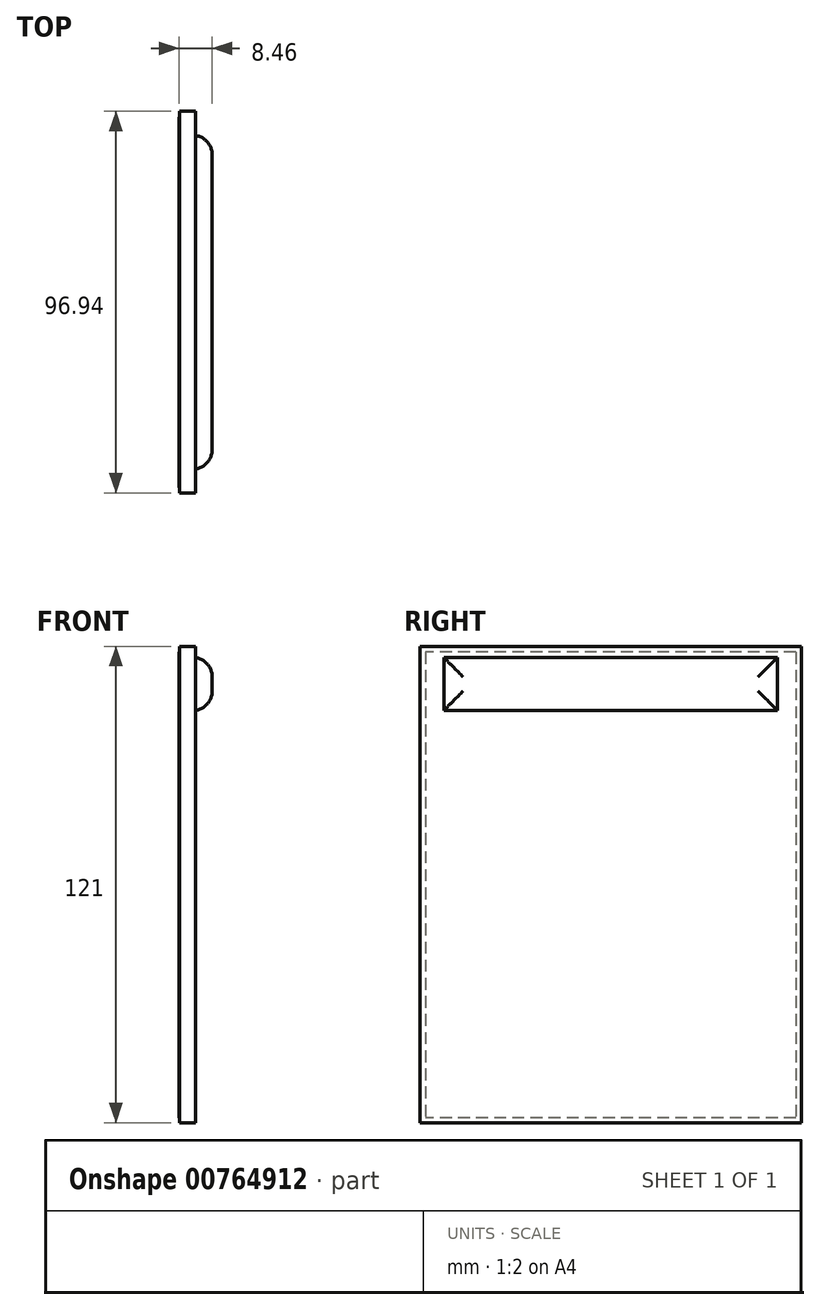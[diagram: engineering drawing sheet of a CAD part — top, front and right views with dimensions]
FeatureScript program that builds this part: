
annotation { "Feature Type Name" : "Feature", "Feature Type Description" : "" }
export const myFeature = defineFeature(function(context is Context, id is Id, definition is map)
    precondition{}
    {
        {
            var Q0;
            Q0=qCreatedBy(makeId("Top.planeOp"),FACE);
            var sketch = newSketch(context, id + "F0", { "sketchPlane" : qUnion([Q0])});
            skLineSegment(sketch, "E0.bottom", {"start": v(-2.03, 48.47) * mm, "end": v(2.03, 48.47) * mm});
            skLineSegment(sketch, "E0.top", {"start": v(-2.03, -48.47) * mm, "end": v(2.03, -48.47) * mm});
            skLineSegment(sketch, "E0.left", {"start": v(-2.03, 48.47) * mm, "end": v(-2.03, -48.47) * mm});
            skLineSegment(sketch, "E0.right", {"start": v(2.03, 48.47) * mm, "end": v(2.03, -48.47) * mm});
            skPoint(sketch, "E0.middle", {"position": v(0, 0) * mm});
            skSolve(sketch);
        }
        {
            var Q0;
            Q0 = qSketchRegion(id + "F0", true);
            extrude(context, id + "F1", {"entities" : qUnion([Q0]), "depth" : 121 * mm, "offsetDistance" : 25 * mm});
        }
        {
            var Q0;
            Q0=makeQuery(id+"F1.opExtrude","SWEPT_FACE",FACE,{"disambiguationData":[OSD([sQuery(id+"F0.wireOp",EDGE,"E0.left")])]});
            var sketch = newSketch(context, id + "F2", { "sketchPlane" : qUnion([Q0])});
            skLineSegment(sketch, "E1.bottom", {"start": v(-47.06, 119.58) * mm, "end": v(47.06, 119.58) * mm});
            skLineSegment(sketch, "E1.top", {"start": v(-47.06, 1.27) * mm, "end": v(47.06, 1.27) * mm});
            skLineSegment(sketch, "E1.left", {"start": v(-47.06, 119.58) * mm, "end": v(-47.06, 1.27) * mm});
            skLineSegment(sketch, "E1.right", {"start": v(47.06, 119.58) * mm, "end": v(47.06, 1.27) * mm});
            skPoint(sketch, "E1.middle", {"position": v(0, 60.42) * mm});
            skSolve(sketch);
        }
        {
            var Q0;
            Q0 = qSketchRegion(id + "F2", true);
            extrude(context, id + "F3", {"entities" : qUnion([Q0]), "operationType" : NewBodyOperationType.ADD, "depth" : 0.2 * mm, "offsetDistance" : 25 * mm});
        }
        {
            var Q0;
            Q0=makeQuery(id+"F1.opExtrude","SWEPT_FACE",FACE,{"disambiguationData":[OSD([sQuery(id+"F0.wireOp",EDGE,"E0.right")])]});
            var sketch = newSketch(context, id + "F4", { "sketchPlane" : qUnion([Q0])});
            skLineSegment(sketch, "E2.bottom", {"start": v(-42.38, 118.17) * mm, "end": v(42.38, 118.17) * mm});
            skLineSegment(sketch, "E2.top", {"start": v(-42.38, 104.75) * mm, "end": v(42.38, 104.75) * mm});
            skLineSegment(sketch, "E2.left", {"start": v(-42.38, 118.17) * mm, "end": v(-42.38, 104.75) * mm});
            skLineSegment(sketch, "E2.right", {"start": v(42.38, 118.17) * mm, "end": v(42.38, 104.75) * mm});
            skPoint(sketch, "E2.middle", {"position": v(0, 111.46) * mm});
            skSolve(sketch);
        }
        {
            var Q0;
            Q0 = qSketchRegion(id + "F4", true);
            extrude(context, id + "F5", {"entities" : qUnion([Q0]), "operationType" : NewBodyOperationType.ADD, "depth" : 4.2 * mm, "offsetDistance" : 25 * mm});
        }
        {
            var Q0;
            Q0=makeQuery(id+"F5.opExtrude","CAP_FACE",FACE,{"disambiguationData":[OSD([sQuery(id+"F4.wireOp",EDGE,"E2.bottom"),sQuery(id+"F4.wireOp",EDGE,"E2.top"),sQuery(id+"F4.wireOp",EDGE,"E2.left"),sQuery(id+"F4.wireOp",EDGE,"E2.right")])],"isStart":false});
            fillet(context, id + "F6", {"entities" : qUnion([Q0]), "radius" : 5 * mm, "tangentPropagation" : true, "allowEdgeOverflow" : false});
        }
    });
